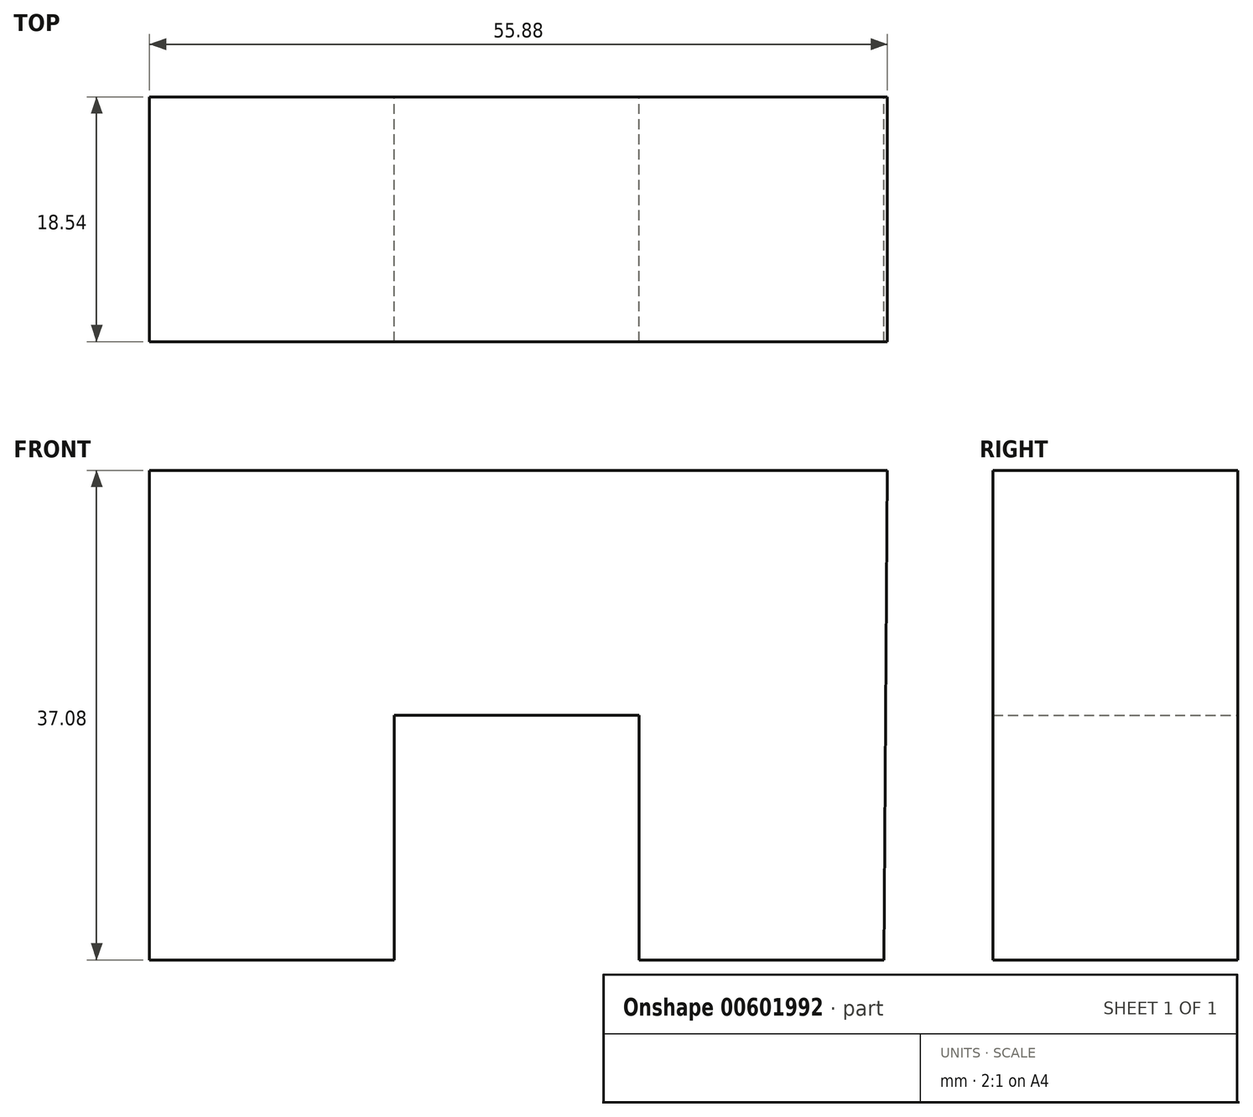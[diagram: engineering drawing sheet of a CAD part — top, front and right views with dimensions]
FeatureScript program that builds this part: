
annotation { "Feature Type Name" : "Feature", "Feature Type Description" : "" }
export const myFeature = defineFeature(function(context is Context, id is Id, definition is map)
    precondition{}
    {
        {
            var Q0;
            Q0=qCreatedBy(makeId("Front.planeOp"),FACE);
            var sketch = newSketch(context, id + "F0", { "sketchPlane" : qUnion([Q0])});
            skLineSegment(sketch, "E0", {"start": v(-23.43, 29.85) * mm, "end": v(-23.43, -7.23) * mm});
            skLineSegment(sketch, "E1", {"start": v(-23.43, -7.23) * mm, "end": v(-4.88, -7.23) * mm});
            skLineSegment(sketch, "E2", {"start": v(-4.88, -7.23) * mm, "end": v(-4.88, 11.31) * mm});
            skLineSegment(sketch, "E3", {"start": v(-4.88, 11.31) * mm, "end": v(13.66, 11.31) * mm});
            skLineSegment(sketch, "E4", {"start": v(13.66, 11.31) * mm, "end": v(13.66, -7.23) * mm});
            skLineSegment(sketch, "E5", {"start": v(13.66, -7.23) * mm, "end": v(32.2, -7.23) * mm});
            skLineSegment(sketch, "E6", {"start": v(-23.43, 29.85) * mm, "end": v(32.45, 29.85) * mm});
            skLineSegment(sketch, "E7", {"start": v(32.45, 29.85) * mm, "end": v(32.2, -7.23) * mm});
            skSolve(sketch);
        }
        {
            var Q0;
            Q0=makeQuery(id+"F0.imprint","IMPRINT",FACE,{"disambiguationData":[TD([[makeQuery(id+"F0.imprint","IMPRINT",EDGE,{"derivedFrom":sQuery(id+"F0.wireOp",EDGE,"E0")}),1.0]])]});
            extrude(context, id + "F1", {"entities" : qUnion([Q0]), "depth" : 18.54 * mm, "offsetDistance" : 25 * mm});
        }
    });
